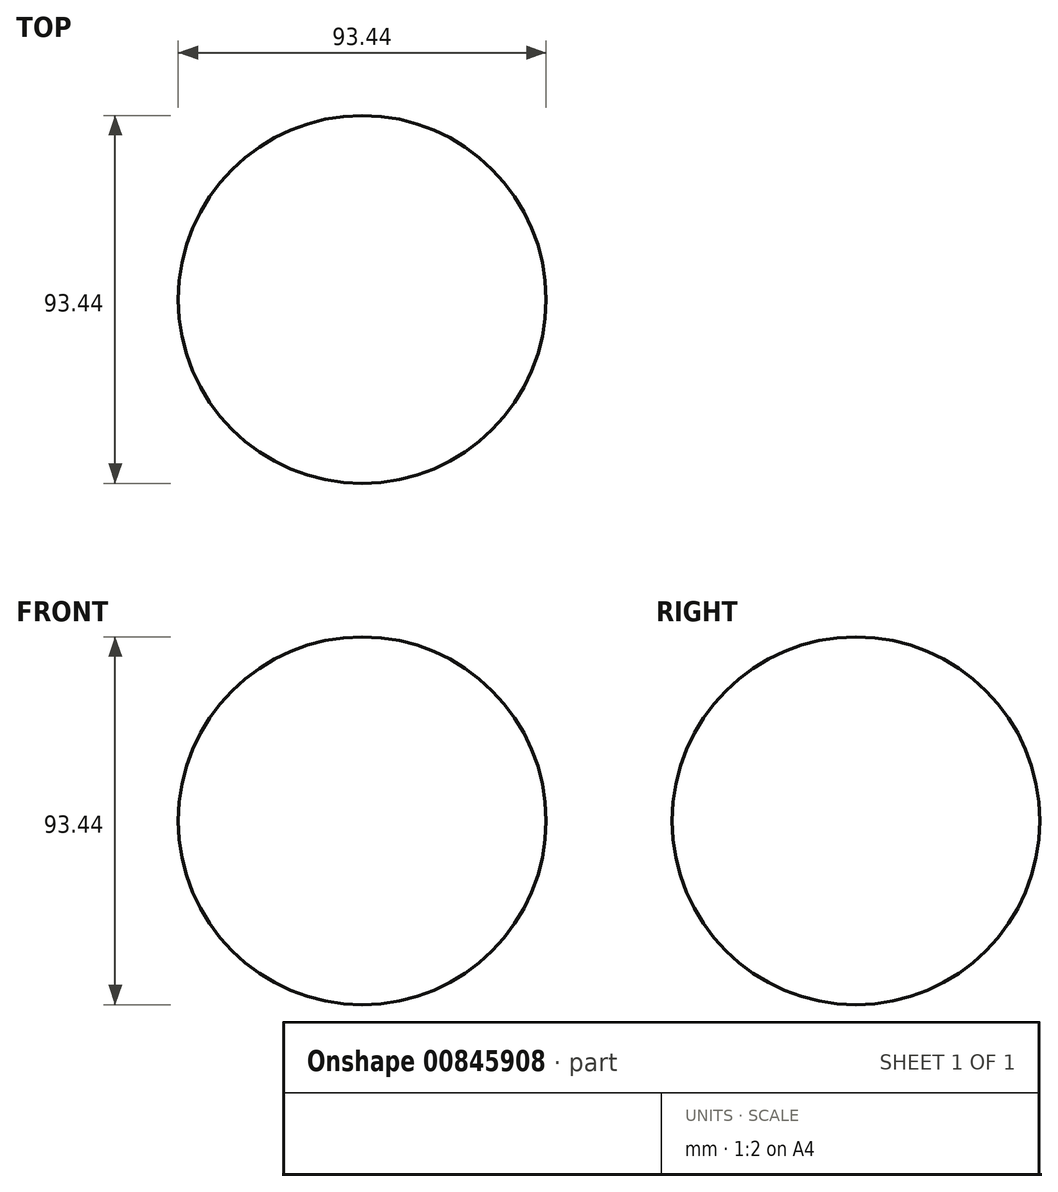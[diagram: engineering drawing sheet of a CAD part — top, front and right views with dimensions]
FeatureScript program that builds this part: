
annotation { "Feature Type Name" : "Feature", "Feature Type Description" : "" }
export const myFeature = defineFeature(function(context is Context, id is Id, definition is map)
    precondition{}
    {
        {
            var Q0;
            Q0=qCreatedBy(makeId("Front.planeOp"),FACE);
            var sketch = newSketch(context, id + "F0", { "sketchPlane" : qUnion([Q0])});
            skCircle(sketch, "E0", {"center": v(0, 0) * mm, "radius": 46.72 * mm});
            skLineSegment(sketch, "E1", {"start": v(0, 57.87) * mm, "end": v(0, -73.28) * mm});
            skSolve(sketch);
        }
        {
            var Q0;
            {var subQ0=sQuery(id+"F0.wireOp",EDGE,"E1");var subQ1=sQuery(id+"F0.wireOp",EDGE,"E0");var subQ2=makeQuery(id+"F0.imprint","INTERSECT",VERTEX,{"disambiguationData":[OD(0.0)],"derivedFrom":[subQ1,subQ0]});Q0=makeQuery(id+"F0.imprint","IMPRINT",FACE,{"disambiguationData":[TD([[makeQuery(id+"F0.imprint","IMPRINT",EDGE,{"disambiguationData":[TD([[subQ2,-1.0]])],"derivedFrom":subQ1}),1.0]])]});}
            var Q1;
            Q1=sQuery(id+"F0.wireOp",EDGE,"E1");
            revolve(context, id + "F1", {"surfaceOperationType" : NewSurfaceOperationType.NEW, "entities" : qUnion([Q0]), "axis" : qUnion([Q1]), "revolveType" : RevolveType.FULL});
        }
    });
